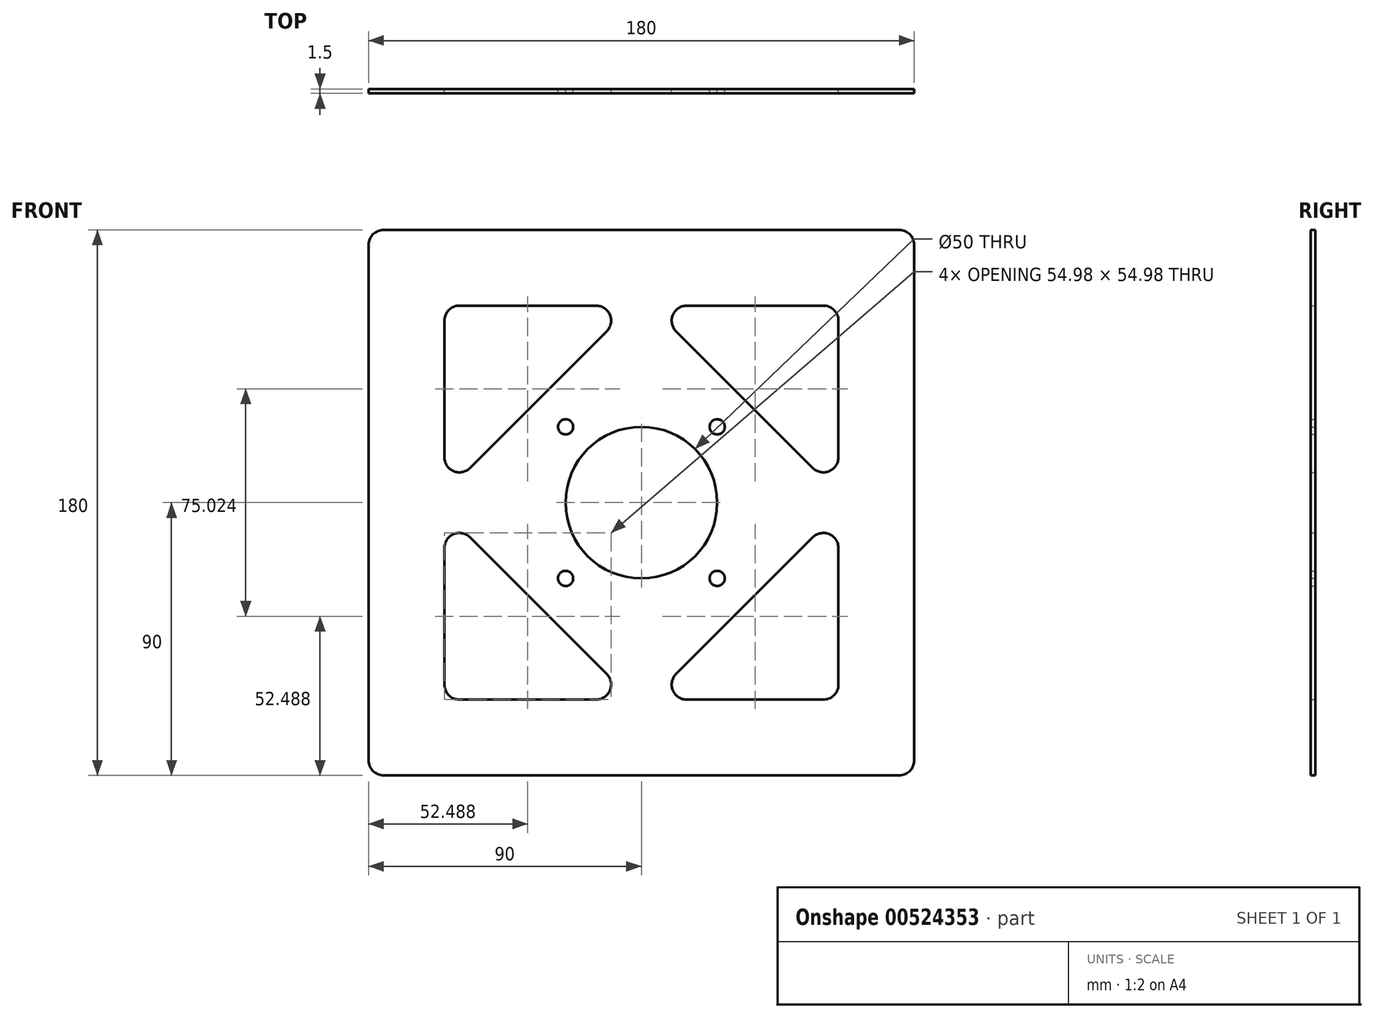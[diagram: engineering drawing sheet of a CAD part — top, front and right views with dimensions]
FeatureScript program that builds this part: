
annotation { "Feature Type Name" : "Feature", "Feature Type Description" : "" }
export const myFeature = defineFeature(function(context is Context, id is Id, definition is map)
    precondition{}
    {
        {
            var Q0;
            Q0=qCreatedBy(makeId("Front.planeOp"),FACE);
            var sketch = newSketch(context, id + "F0", { "sketchPlane" : qUnion([Q0])});
            skLineSegment(sketch, "E0.bottom", {"start": v(5, 0) * mm, "end": v(175, 0) * mm});
            skLineSegment(sketch, "E0.top", {"start": v(5, 180) * mm, "end": v(175, 180) * mm});
            skLineSegment(sketch, "E0.left", {"start": v(0, 5) * mm, "end": v(0, 175) * mm});
            skLineSegment(sketch, "E0.right", {"start": v(180, 5) * mm, "end": v(180, 175) * mm});
            skPoint(sketch, "E1.visualSharp", {"position": v(0, 180) * mm});
            skArc(sketch, "E1.filletArc", {"start": v(5, 180) * mm, "mid": v(1.46, 178.54) * mm, "end": v(0, 175) * mm});
            skPoint(sketch, "E2.visualSharp", {"position": v(0, 0) * mm});
            skArc(sketch, "E2.filletArc", {"start": v(0, 5) * mm, "mid": v(1.46, 1.46) * mm, "end": v(5, 0) * mm});
            skPoint(sketch, "E3.visualSharp", {"position": v(180, 0) * mm});
            skArc(sketch, "E3.filletArc", {"start": v(175, 0) * mm, "mid": v(178.54, 1.46) * mm, "end": v(180, 5) * mm});
            skPoint(sketch, "E4.visualSharp", {"position": v(180, 180) * mm});
            skArc(sketch, "E4.filletArc", {"start": v(180, 175) * mm, "mid": v(178.54, 178.54) * mm, "end": v(175, 180) * mm});
            skCircle(sketch, "E5", {"center": v(90, 90) * mm, "radius": 25 * mm});
            skPoint(sketch, "E5.centerSnap0", {"position": v(0, 90) * mm});
            skPoint(sketch, "E5.centerSnap1", {"position": v(90, 180) * mm});
            skLineSegment(sketch, "E6.bottom", {"start": v(30, 155) * mm, "end": v(75, 155) * mm});
            skLineSegment(sketch, "E6.left", {"start": v(25, 150) * mm, "end": v(25, 105) * mm});
            skLineSegment(sketch, "E7", {"start": v(33.54, 101.46) * mm, "end": v(78.54, 146.46) * mm});
            skPoint(sketch, "E8.visualSharp", {"position": v(25, 155) * mm});
            skArc(sketch, "E8.filletArc", {"start": v(30, 155) * mm, "mid": v(26.46, 153.54) * mm, "end": v(25, 150) * mm});
            skArc(sketch, "E9.filletArc", {"start": v(78.54, 146.46) * mm, "mid": v(79.62, 151.91) * mm, "end": v(75, 155) * mm});
            skArc(sketch, "E10.filletArc", {"start": v(25, 105) * mm, "mid": v(28.09, 100.38) * mm, "end": v(33.54, 101.46) * mm});
            skLineSegment(sketch, "E11", {"start": v(90, 90) * mm, "end": v(0, 90) * mm, "construction": true});
            skLineSegment(sketch, "E12.MirrorCS", {"start": v(33.54, 78.54) * mm, "end": v(78.54, 33.54) * mm});
            skArc(sketch, "E13.MirrorCS", {"start": v(25, 75) * mm, "mid": v(28.09, 79.62) * mm, "end": v(33.54, 78.54) * mm});
            skLineSegment(sketch, "E14.MirrorCS", {"start": v(25, 30) * mm, "end": v(25, 75) * mm});
            skArc(sketch, "E15.MirrorCS", {"start": v(30, 25) * mm, "mid": v(26.46, 26.46) * mm, "end": v(25, 30) * mm});
            skLineSegment(sketch, "E16.MirrorCS", {"start": v(30, 25) * mm, "end": v(75, 25) * mm});
            skArc(sketch, "E17.MirrorCS", {"start": v(78.54, 33.54) * mm, "mid": v(79.62, 28.09) * mm, "end": v(75, 25) * mm});
            skLineSegment(sketch, "E18", {"start": v(90, 90) * mm, "end": v(90, 180) * mm, "construction": true});
            skLineSegment(sketch, "E19.MirrorCS", {"start": v(146.46, 101.46) * mm, "end": v(101.46, 146.46) * mm});
            skArc(sketch, "E20.MirrorCS", {"start": v(155, 105) * mm, "mid": v(151.91, 100.38) * mm, "end": v(146.46, 101.46) * mm});
            skLineSegment(sketch, "E21.MirrorCS", {"start": v(155, 150) * mm, "end": v(155, 105) * mm});
            skArc(sketch, "E22.MirrorCS", {"start": v(150, 155) * mm, "mid": v(153.54, 153.54) * mm, "end": v(155, 150) * mm});
            skLineSegment(sketch, "E23.MirrorCS", {"start": v(150, 155) * mm, "end": v(105, 155) * mm});
            skArc(sketch, "E24.MirrorCS", {"start": v(101.46, 146.46) * mm, "mid": v(100.38, 151.91) * mm, "end": v(105, 155) * mm});
            skLineSegment(sketch, "E25.MirrorCS", {"start": v(146.46, 78.54) * mm, "end": v(101.46, 33.54) * mm});
            skArc(sketch, "E26.MirrorCS", {"start": v(155, 75) * mm, "mid": v(151.91, 79.62) * mm, "end": v(146.46, 78.54) * mm});
            skLineSegment(sketch, "E27.MirrorCS", {"start": v(155, 30) * mm, "end": v(155, 75) * mm});
            skArc(sketch, "E28.MirrorCS", {"start": v(150, 25) * mm, "mid": v(153.54, 26.46) * mm, "end": v(155, 30) * mm});
            skLineSegment(sketch, "E29.MirrorCS", {"start": v(150, 25) * mm, "end": v(105, 25) * mm});
            skArc(sketch, "E30.MirrorCS", {"start": v(101.46, 33.54) * mm, "mid": v(100.38, 28.09) * mm, "end": v(105, 25) * mm});
            skLineSegment(sketch, "E31.bottom", {"start": v(90, 90) * mm, "end": v(115, 90) * mm, "construction": true});
            skLineSegment(sketch, "E31.left", {"start": v(90, 90) * mm, "end": v(90, 115) * mm, "construction": true});
            skCircle(sketch, "E32", {"center": v(115, 115) * mm, "radius": 2.5 * mm});
            skCircle(sketch, "E33.MirrorC", {"center": v(65, 115) * mm, "radius": 2.5 * mm});
            skCircle(sketch, "E34.MirrorC", {"center": v(115, 65) * mm, "radius": 2.5 * mm});
            skCircle(sketch, "E35.MirrorC", {"center": v(65, 65) * mm, "radius": 2.5 * mm});
            skSolve(sketch);
        }
        {
            var Q0;
            Q0 = qSketchRegion(id + "F0", true);
            extrude(context, id + "F1", {"entities" : qUnion([Q0]), "depth" : 1.5 * mm, "offsetDistance" : 25 * mm});
        }
    });
